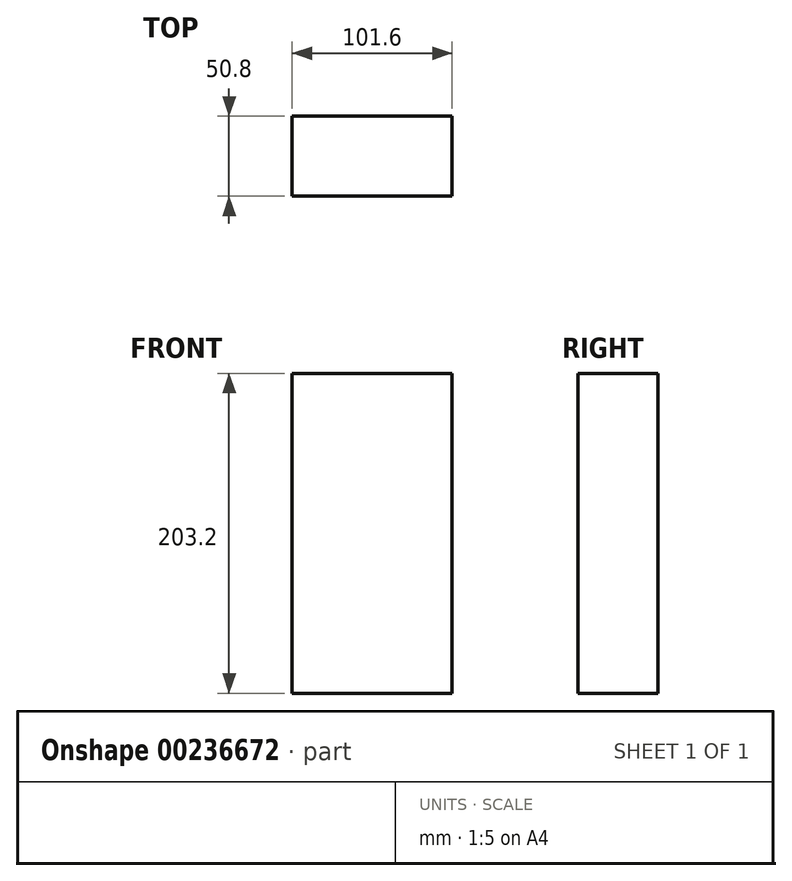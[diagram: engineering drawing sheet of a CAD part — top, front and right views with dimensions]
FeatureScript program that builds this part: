
annotation { "Feature Type Name" : "Feature", "Feature Type Description" : "" }
export const myFeature = defineFeature(function(context is Context, id is Id, definition is map)
    precondition{}
    {
        {
            var Q0;
            Q0=qCreatedBy(makeId("Front.planeOp"),FACE);
            var sketch = newSketch(context, id + "F0", { "sketchPlane" : qUnion([Q0])});
            skLineSegment(sketch, "E0.bottom", {"start": v(-50.8, 101.6) * mm, "end": v(50.8, 101.6) * mm});
            skLineSegment(sketch, "E0.top", {"start": v(-50.8, -101.6) * mm, "end": v(50.8, -101.6) * mm});
            skLineSegment(sketch, "E0.left", {"start": v(-50.8, 101.6) * mm, "end": v(-50.8, -101.6) * mm});
            skLineSegment(sketch, "E0.right", {"start": v(50.8, 101.6) * mm, "end": v(50.8, -101.6) * mm});
            skPoint(sketch, "E0.middle", {"position": v(0, 0) * mm});
            skSolve(sketch);
        }
        {
            var Q0;
            Q0 = qSketchRegion(id + "F0", true);
            extrude(context, id + "F1", {"entities" : qUnion([Q0]), "endBound" : BoundingType.SYMMETRIC, "depth" : 50.8 * mm});
        }
    });
